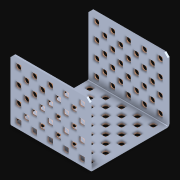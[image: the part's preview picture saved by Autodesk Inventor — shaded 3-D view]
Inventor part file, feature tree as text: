
AUTODESK INVENTOR PART (.ipt)
format: ipt  version: 2021 (Build 250183000, 183)  size: 1,171,456 bytes
history: native  units: in
note: dims shown in document units (in); Inventor stores cm internally (conversion verified against a paired STEP export)
features: other x106, extrude x105, pattern_linear x6, sketch x3, imported_body x1
ambient origin geometry x8: Origin, YZ Plane, XZ Plane, XY Plane, X Axis, Y Axis, Z Axis, Center Point
bodies: Body1 (feature_tree), Body2 (feature_tree), Body3 (feature_tree), Body4 (feature_tree), Body5 (feature_tree), Body6 (feature_tree), Body7 (feature_tree), Body8 (feature_tree), Body9 (feature_tree), Body10 (feature_tree), Body11 (feature_tree), Body12 (feature_tree), Body13 (feature_tree), Body14 (feature_tree), Body15 (feature_tree), Body16 (feature_tree), Body17 (feature_tree), Body18 (feature_tree), Body19 (feature_tree), Body20 (feature_tree), Body21 (feature_tree), Body22 (feature_tree), Body23 (feature_tree), Body24 (feature_tree), Body25 (feature_tree), Body26 (feature_tree), Body27 (feature_tree), Body28 (feature_tree), Body29 (feature_tree), Body30 (feature_tree), Body31 (feature_tree), Body32 (feature_tree), Body33 (feature_tree), Body34 (feature_tree), Body35 (feature_tree), Body36 (feature_tree), Body37 (feature_tree), Body38 (feature_tree), Body39 (feature_tree), Body40 (feature_tree), Body41 (feature_tree), Body42 (feature_tree), Body43 (feature_tree), Body44 (feature_tree), Body45 (feature_tree), Body46 (feature_tree), Body47 (feature_tree), Body48 (feature_tree), Body49 (feature_tree), Body50 (feature_tree), Body51 (feature_tree), Body52 (feature_tree), Body53 (feature_tree), Body54 (feature_tree), Body55 (feature_tree), Body56 (feature_tree), Body57 (feature_tree), Body58 (feature_tree), Body59 (feature_tree), Body60 (feature_tree), Body61 (feature_tree), Body62 (feature_tree), Body63 (feature_tree), Body64 (feature_tree), Body65 (feature_tree), Body66 (feature_tree), Body67 (feature_tree), Body68 (feature_tree), Body69 (feature_tree), Body70 (feature_tree), Body71 (feature_tree), Body72 (feature_tree), Body73 (feature_tree), Body74 (feature_tree), Body75 (feature_tree), Body76 (feature_tree), Body77 (feature_tree), Body78 (feature_tree), Body79 (feature_tree), Body80 (feature_tree), Body81 (feature_tree), Body82 (feature_tree), Body83 (feature_tree), Body84 (feature_tree), Body85 (feature_tree), Body86 (feature_tree), Body87 (feature_tree), Body88 (feature_tree), Body89 (feature_tree), Body90 (feature_tree), Body91 (feature_tree), Body92 (feature_tree), Body93 (feature_tree), Body94 (feature_tree), Body95 (feature_tree), Body96 (feature_tree), Body97 (feature_tree), Body98 (feature_tree), Body99 (feature_tree), Body100 (feature_tree), Body101 (feature_tree), Body102 (feature_tree), Body103 (feature_tree), Body104 (feature_tree), Body105 (feature_tree), Body106 (feature_tree)
feature tree (221):
  other  "LPattern4"
  imported_body  "Base1"
  pattern_linear  "Rectangular Pattern1"  Count1=4 Spacing1=0.5in
  pattern_linear  "Rectangular Pattern2"  Count1=5 Spacing1=0.5in
  pattern_linear  "Rectangular Pattern3"  Count1=3 Spacing1=0.5in
  pattern_linear  "Rectangular Pattern4"  Count1=4 Spacing1=0.5in
  pattern_linear  "Rectangular Pattern5"  Count1=4 Spacing1=0.5in
  pattern_linear  "Rectangular Pattern6"  Count1=5 Spacing1=0.5in
  other  "Srf1"
  other  "Srf2"
  other  "Srf3"
  other  "Srf4"
  other  "Srf5"
  other  "Srf6"
  other  "Srf7"
  other  "Srf8"
  other  "Srf9"
  other  "Srf10"
  other  "Srf11"
  other  "Srf12"
  other  "Srf13"
  other  "Srf14"
  other  "Srf15"
  other  "Srf16"
  other  "Srf17"
  other  "Srf18"
  other  "Srf19"
  other  "Srf20"
  other  "Srf21"
  other  "Srf22"
  other  "Srf23"
  other  "Srf24"
  other  "Srf25"
  other  "Srf26"
  other  "Srf27"
  other  "Srf28"
  other  "Srf29"
  other  "Srf30"
  other  "Srf31"
  other  "Srf32"
  other  "Srf33"
  other  "Srf34"
  other  "Srf35"
  other  "Srf36"
  other  "Srf37"
  other  "Srf38"
  other  "Srf39"
  other  "Srf40"
  other  "Srf41"
  other  "Srf42"
  other  "Srf43"
  other  "Srf44"
  other  "Srf45"
  other  "Srf46"
  other  "Srf47"
  other  "Srf48"
  other  "Srf49"
  other  "Srf50"
  other  "Srf51"
  other  "Srf52"
  sketch  "Sketch4"  dims[d49=0.046in d50=0.0in d51=1.5748in d53=0.5in d54=1.9685in d56=0.5in]
  other  "Srf53"
  other  "Srf54"
  other  "Srf55"
  other  "Srf56"
  other  "Srf57"
  other  "Srf58"
  other  "Srf59"
  other  "Srf60"
  other  "Srf61"
  other  "Srf62"
  other  "Srf63"
  other  "Srf64"
  sketch  "Sketch5"  dims[d58=0.046in d59=0.0in d60=1.1811in d62=0.5in d63=1.5748in d65=0.5in]
  other  "Srf65"
  other  "Srf66"
  other  "Srf67"
  other  "Srf68"
  other  "Srf69"
  other  "Srf70"
  other  "Srf71"
  other  "Srf72"
  other  "Srf73"
  other  "Srf74"
  other  "Srf75"
  other  "Srf76"
  other  "Srf77"
  other  "Srf78"
  other  "Srf79"
  other  "Srf80"
  other  "Srf81"
  other  "Srf82"
  other  "Srf83"
  other  "Srf84"
  other  "Srf85"
  other  "Srf86"
  other  "Srf87"
  other  "Srf88"
  other  "Srf89"
  sketch  "Sketch6"  dims[d67=0.046in d68=0.0in d69=1.5748in d71=0.5in d72=1.9685in d74=0.5in d76=0.046in d77=0.0in d78=1.1811in d80=0.5in d81=1.5748in d83=0.5in d85=0.046in d86=0.0in d87=1.9685in d89=0.5in d90=1.9685in d92=0.5in d94=0.046in d95=0.0in d96=1.5748in d98=0.5in d99=1.5748in d101=0.5in d102=0.0in d103=0.0in d104=0.0in d105=0.0in d106=0.0in d107=0.0in d108=0.0in d109=0.0in d110=0.0in d111=0.0in d112=0.0in d113=0.0in d114=0.0in d115=0.0in d116=0.0in d117=0.0in d118=0.0in d119=0.0in d120=0.0in d121=0.0in d122=0.0in d123=0.0in d124=0.0in d125=0.0in d126=0.0in d127=0.0in d128=0.0in d129=0.0in d130=0.0in d131=0.0in d132=0.0in d133=0.0in d134=0.0in d135=0.0in d136=0.0in d137=0.0in d138=0.0in d139=0.0in d140=0.0in d141=0.0in d142=0.0in d143=0.0in d144=0.0in d145=0.0in d146=0.0in d147=0.0in d148=0.0in d149=0.0in d150=0.0in d151=0.0in d152=0.0in d153=0.0in d154=0.0in d155=0.0in d156=0.0in d157=0.0in d158=0.0in d159=0.0in d160=0.0in d161=0.0in d162=0.0in d163=0.0in d164=0.0in d165=0.0in d166=0.0in d167=0.0in d168=0.0in d169=0.0in d170=0.0in d171=0.0in d172=0.0in d173=0.0in d174=0.0in d175=0.0in d176=0.0in d177=0.0in d178=0.0in d179=0.0in d180=0.0in d181=0.0in d182=0.0in d183=0.0in d184=0.0in d185=0.0in d186=0.0in d187=0.0in d188=0.0in d189=0.0in d190=0.0in d191=0.0in d192=0.0in d193=0.0in d194=0.0in d195=0.0in d196=0.0in d197=0.0in d198=0.0in d199=0.0in d200=0.0in d201=0.0in d202=0.0in d203=0.0in d204=0.0in d205=0.0in d206=0.0in d207=0.0in d208=0.0in d209=0.0in d210=0.0in d211=0.0in d212=0.0in d213=0.0in d214=0.0in d215=0.0in d216=0.0in d217=0.0in d218=0.0in d219=0.0in d220=0.0in d221=0.0in d222=0.0in d223=0.0in d224=0.0in d225=0.0in d226=0.0in d227=0.0in d228=0.0in d229=0.0in d230=0.0in d231=0.0in d232=0.0in d233=0.0in d234=0.0in d235=0.0in d236=0.0in d237=0.0in d238=0.0in d239=0.0in d240=0.0in d241=0.0in d242=0.0in d243=0.0in d244=0.0in d245=0.0in d246=0.0in d247=0.0in d248=0.0in d249=0.0in d250=0.0in d251=0.0in d252=0.0in d253=0.0in d254=0.0in d255=0.0in d256=0.0in d257=0.0in d258=0.0in d259=0.0in d260=0.0in d261=0.0in d262=0.0in d263=0.0in d264=0.0in d265=0.0in d266=0.0in d267=0.0in d268=0.0in d269=0.0in d270=0.0in d271=0.0in d272=0.0in d273=0.0in d274=0.0in d275=0.0in d276=0.0in d277=0.0in d278=0.0in d279=0.0in d280=0.0in d281=0.0in d282=0.0in d283=0.0in d284=0.0in d285=0.0in d286=0.0in d287=0.0in d288=0.0in d289=0.0in d290=0.0in d291=0.0in d292=0.0in d293=0.0in d294=0.0in d295=0.0in d296=0.0in d297=0.0in d298=0.0in d299=0.0in d300=0.0in d301=0.0in d302=0.0in d303=0.0in d304=0.0in d305=0.0in d306=0.0in d307=0.0in d308=0.0in d309=0.0in d310=0.0in d311=0.0in]
  other  "Srf90"
  other  "Srf91"
  other  "Srf92"
  other  "Srf93"
  other  "Srf94"
  other  "Srf95"
  other  "Srf96"
  other  "Srf97"
  other  "Srf98"
  other  "Srf99"
  other  "Srf100"
  other  "Srf101"
  other  "Srf102"
  other  "Srf103"
  other  "Srf104"
  other  "Srf105"
  extrude  "ExtrusionSrf1"  Depth=0.5in TaperAngle=0.0deg
  extrude  "ExtrusionSrf21"  Depth=0.5in
  extrude  "ExtrusionSrf33"  Depth=0.5in
  extrude  "ExtrusionSrf53"  Depth=0.5in TaperAngle=0.0deg
  extrude  "ExtrusionSrf65"  Depth=0.5in
  extrude  "ExtrusionSrf90"  Depth=0.5in
  extrude  "ExtrusionSrf2"  Depth=0.5in TaperAngle=0.0deg
  extrude  "ExtrusionSrf3"  Depth=0.5in
  extrude  "ExtrusionSrf4"  Depth=0.5in
  extrude  "ExtrusionSrf5"  TaperAngle=0.0deg  [1 undecoded]
  extrude  "ExtrusionSrf6"  TaperAngle=0.0deg  [1 undecoded]
  extrude  "ExtrusionSrf7"  TaperAngle=0.0deg  [1 undecoded]
  extrude  "ExtrusionSrf8"  TaperAngle=0.0deg  [1 undecoded]
  extrude  "ExtrusionSrf9"  TaperAngle=0.0deg  [1 undecoded]
  extrude  "ExtrusionSrf10"  TaperAngle=0.0deg  [1 undecoded]
  extrude  "ExtrusionSrf11"  TaperAngle=0.0deg  [1 undecoded]
  extrude  "ExtrusionSrf12"  TaperAngle=0.0deg  [1 undecoded]
  extrude  "ExtrusionSrf13"  TaperAngle=0.0deg  [1 undecoded]
  extrude  "ExtrusionSrf14"  TaperAngle=0.0deg  [1 undecoded]
  extrude  "ExtrusionSrf15"  TaperAngle=0.0deg  [1 undecoded]
  extrude  "ExtrusionSrf16"  TaperAngle=0.0deg  [1 undecoded]
  extrude  "ExtrusionSrf17"  TaperAngle=0.0deg  [1 undecoded]
  extrude  "ExtrusionSrf18"  TaperAngle=0.0deg  [1 undecoded]
  extrude  "ExtrusionSrf19"  TaperAngle=0.0deg  [1 undecoded]
  extrude  "ExtrusionSrf20"  TaperAngle=0.0deg  [1 undecoded]
  extrude  "ExtrusionSrf22"  TaperAngle=0.0deg  [1 undecoded]
  extrude  "ExtrusionSrf23"  TaperAngle=0.0deg  [1 undecoded]
  extrude  "ExtrusionSrf24"  TaperAngle=0.0deg  [1 undecoded]
  extrude  "ExtrusionSrf25"  TaperAngle=0.0deg  [1 undecoded]
  extrude  "ExtrusionSrf26"  TaperAngle=0.0deg  [1 undecoded]
  extrude  "ExtrusionSrf27"  TaperAngle=0.0deg  [1 undecoded]
  extrude  "ExtrusionSrf28"  TaperAngle=0.0deg  [1 undecoded]
  extrude  "ExtrusionSrf29"  TaperAngle=0.0deg  [1 undecoded]
  extrude  "ExtrusionSrf30"  TaperAngle=0.0deg  [1 undecoded]
  extrude  "ExtrusionSrf31"  TaperAngle=0.0deg  [1 undecoded]
  extrude  "ExtrusionSrf32"  TaperAngle=0.0deg  [1 undecoded]
  extrude  "ExtrusionSrf34"  TaperAngle=0.0deg  [1 undecoded]
  extrude  "ExtrusionSrf35"  TaperAngle=0.0deg  [1 undecoded]
  extrude  "ExtrusionSrf36"  TaperAngle=0.0deg  [1 undecoded]
  extrude  "ExtrusionSrf37"  TaperAngle=0.0deg  [1 undecoded]
  extrude  "ExtrusionSrf38"  TaperAngle=0.0deg  [1 undecoded]
  extrude  "ExtrusionSrf39"  TaperAngle=0.0deg  [1 undecoded]
  extrude  "ExtrusionSrf40"  TaperAngle=0.0deg  [1 undecoded]
  extrude  "ExtrusionSrf41"  TaperAngle=0.0deg  [1 undecoded]
  extrude  "ExtrusionSrf42"  TaperAngle=0.0deg  [1 undecoded]
  extrude  "ExtrusionSrf43"  TaperAngle=0.0deg  [1 undecoded]
  extrude  "ExtrusionSrf44"  TaperAngle=0.0deg  [1 undecoded]
  extrude  "ExtrusionSrf45"  TaperAngle=0.0deg  [1 undecoded]
  extrude  "ExtrusionSrf46"  TaperAngle=0.0deg  [1 undecoded]
  extrude  "ExtrusionSrf47"  TaperAngle=0.0deg  [1 undecoded]
  extrude  "ExtrusionSrf48"  TaperAngle=0.0deg  [1 undecoded]
  extrude  "ExtrusionSrf49"  TaperAngle=0.0deg  [1 undecoded]
  extrude  "ExtrusionSrf50"  TaperAngle=0.0deg  [1 undecoded]
  extrude  "ExtrusionSrf51"  TaperAngle=0.0deg  [1 undecoded]
  extrude  "ExtrusionSrf52"  TaperAngle=0.0deg  [1 undecoded]
  extrude  "ExtrusionSrf54"  TaperAngle=0.0deg  [1 undecoded]
  extrude  "ExtrusionSrf55"  TaperAngle=0.0deg  [1 undecoded]
  extrude  "ExtrusionSrf56"  TaperAngle=0.0deg  [1 undecoded]
  extrude  "ExtrusionSrf57"  TaperAngle=0.0deg  [1 undecoded]
  extrude  "ExtrusionSrf58"  TaperAngle=0.0deg  [1 undecoded]
  extrude  "ExtrusionSrf59"  TaperAngle=0.0deg  [1 undecoded]
  extrude  "ExtrusionSrf60"  TaperAngle=0.0deg  [1 undecoded]
  extrude  "ExtrusionSrf61"  TaperAngle=0.0deg  [1 undecoded]
  extrude  "ExtrusionSrf62"  TaperAngle=0.0deg  [1 undecoded]
  extrude  "ExtrusionSrf63"  TaperAngle=0.0deg  [1 undecoded]
  extrude  "ExtrusionSrf64"  TaperAngle=0.0deg  [1 undecoded]
  extrude  "ExtrusionSrf66"  TaperAngle=0.0deg  [1 undecoded]
  extrude  "ExtrusionSrf67"  TaperAngle=0.0deg  [1 undecoded]
  extrude  "ExtrusionSrf68"  TaperAngle=0.0deg  [1 undecoded]
  extrude  "ExtrusionSrf69"  TaperAngle=0.0deg  [1 undecoded]
  extrude  "ExtrusionSrf70"  TaperAngle=0.0deg  [1 undecoded]
  extrude  "ExtrusionSrf71"  TaperAngle=0.0deg  [1 undecoded]
  extrude  "ExtrusionSrf72"  TaperAngle=0.0deg  [1 undecoded]
  extrude  "ExtrusionSrf73"  TaperAngle=0.0deg  [1 undecoded]
  extrude  "ExtrusionSrf74"  TaperAngle=0.0deg  [1 undecoded]
  extrude  "ExtrusionSrf75"  TaperAngle=0.0deg  [1 undecoded]
  extrude  "ExtrusionSrf76"  TaperAngle=0.0deg  [1 undecoded]
  extrude  "ExtrusionSrf77"  TaperAngle=0.0deg  [1 undecoded]
  extrude  "ExtrusionSrf78"  TaperAngle=0.0deg  [1 undecoded]
  extrude  "ExtrusionSrf79"  TaperAngle=0.0deg  [1 undecoded]
  extrude  "ExtrusionSrf80"  TaperAngle=0.0deg  [1 undecoded]
  extrude  "ExtrusionSrf81"  TaperAngle=0.0deg  [1 undecoded]
  extrude  "ExtrusionSrf82"  TaperAngle=0.0deg  [1 undecoded]
  extrude  "ExtrusionSrf83"  TaperAngle=0.0deg  [1 undecoded]
  extrude  "ExtrusionSrf84"  TaperAngle=0.0deg  [1 undecoded]
  extrude  "ExtrusionSrf85"  TaperAngle=0.0deg  [1 undecoded]
  extrude  "ExtrusionSrf86"  TaperAngle=0.0deg  [1 undecoded]
  extrude  "ExtrusionSrf87"  TaperAngle=0.0deg  [1 undecoded]
  extrude  "ExtrusionSrf88"  TaperAngle=0.0deg  [1 undecoded]
  extrude  "ExtrusionSrf89"  TaperAngle=0.0deg  [1 undecoded]
  extrude  "ExtrusionSrf91"  TaperAngle=0.0deg  [1 undecoded]
  extrude  "ExtrusionSrf92"  TaperAngle=0.0deg  [1 undecoded]
  extrude  "ExtrusionSrf93"  TaperAngle=0.0deg  [1 undecoded]
  extrude  "ExtrusionSrf94"  TaperAngle=0.0deg  [1 undecoded]
  extrude  "ExtrusionSrf95"  TaperAngle=0.0deg  [1 undecoded]
  extrude  "ExtrusionSrf96"  TaperAngle=0.0deg  [1 undecoded]
  extrude  "ExtrusionSrf97"  TaperAngle=0.0deg  [1 undecoded]
  extrude  "ExtrusionSrf98"  TaperAngle=0.0deg  [1 undecoded]
  extrude  "ExtrusionSrf99"  TaperAngle=0.0deg  [1 undecoded]
  extrude  "ExtrusionSrf100"  TaperAngle=0.0deg  [1 undecoded]
  extrude  "ExtrusionSrf101"  TaperAngle=0.0deg  [1 undecoded]
  extrude  "ExtrusionSrf102"  TaperAngle=0.0deg  [1 undecoded]
  extrude  "ExtrusionSrf103"  TaperAngle=0.0deg  [1 undecoded]
  extrude  "ExtrusionSrf104"  TaperAngle=0.0deg  [1 undecoded]
  extrude  "ExtrusionSrf105"  TaperAngle=0.0deg  [1 undecoded]
note: 96 required parameter values undecoded (feature->parameter linkage not recoverable at this tier; creation-order binding heuristic only, values carry confidence <= 0.55)
